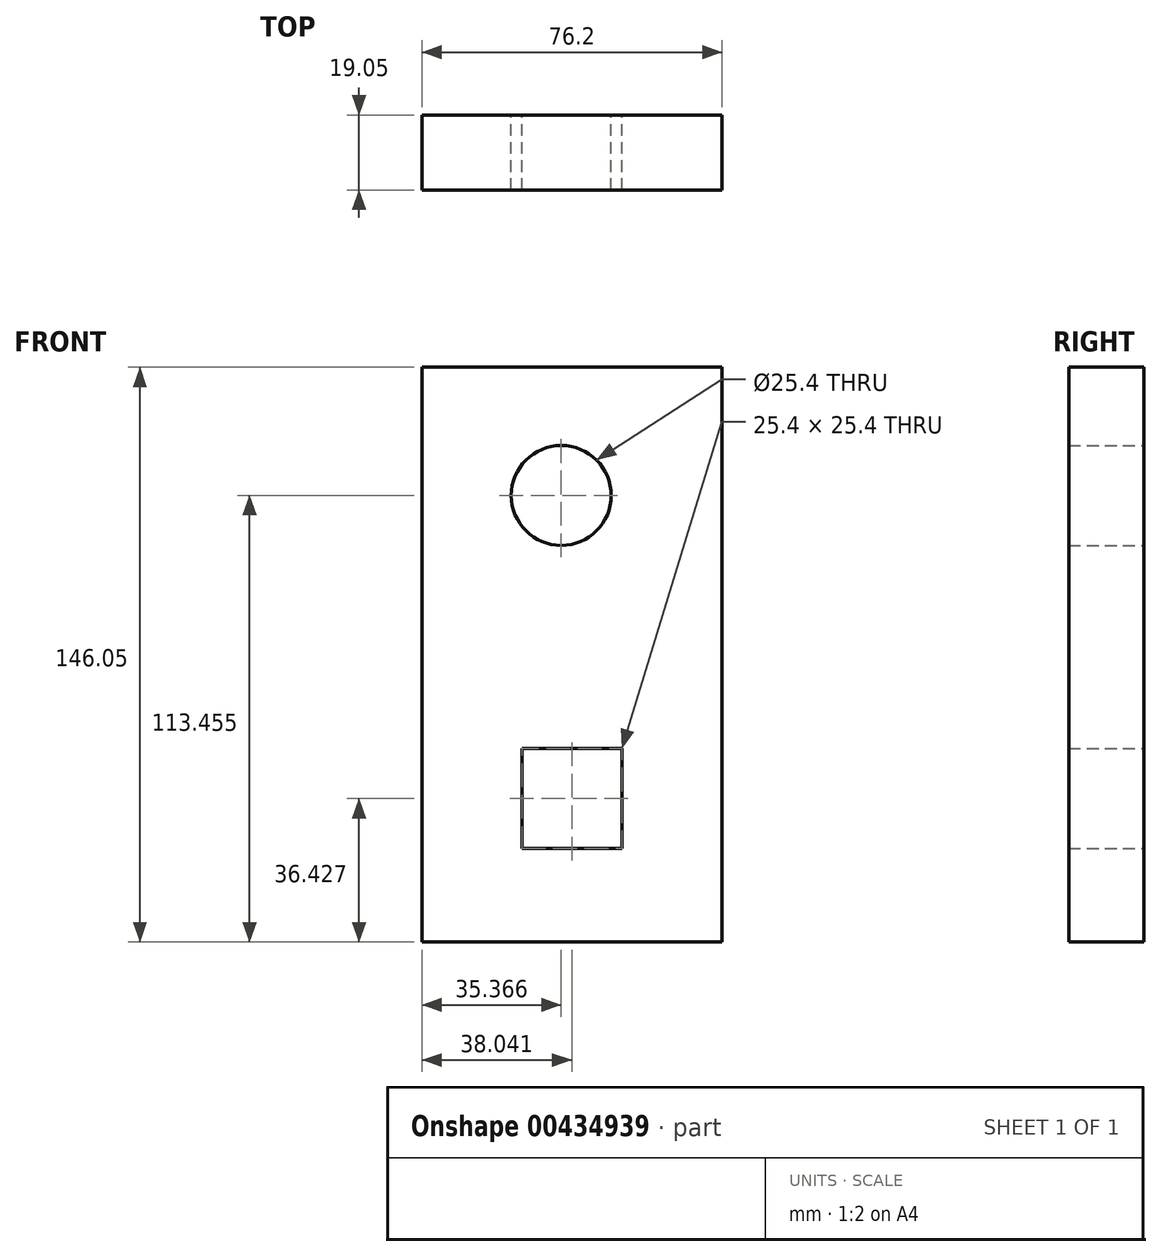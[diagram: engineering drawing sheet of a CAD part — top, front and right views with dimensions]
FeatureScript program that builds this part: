
annotation { "Feature Type Name" : "Feature", "Feature Type Description" : "" }
export const myFeature = defineFeature(function(context is Context, id is Id, definition is map)
    precondition{}
    {
        {
            var Q0;
            Q0=qCreatedBy(makeId("Front.planeOp"),FACE);
            var sketch = newSketch(context, id + "F0", { "sketchPlane" : qUnion([Q0])});
            skLineSegment(sketch, "E0", {"start": v(0, 0) * mm, "end": v(76.2, 0) * mm});
            skLineSegment(sketch, "E1", {"start": v(76.2, 0) * mm, "end": v(76.2, 146.05) * mm});
            skLineSegment(sketch, "E2", {"start": v(76.2, 146.05) * mm, "end": v(0, 146.05) * mm});
            skLineSegment(sketch, "E3", {"start": v(0, 146.05) * mm, "end": v(0, 0) * mm});
            skCircle(sketch, "E4", {"center": v(35.37, 113.46) * mm, "radius": 12.7 * mm});
            skLineSegment(sketch, "E5", {"start": v(25.34, 49.13) * mm, "end": v(50.74, 49.13) * mm});
            skLineSegment(sketch, "E6", {"start": v(50.74, 49.13) * mm, "end": v(50.74, 23.73) * mm});
            skLineSegment(sketch, "E7", {"start": v(50.74, 23.73) * mm, "end": v(25.34, 23.73) * mm});
            skLineSegment(sketch, "E8", {"start": v(25.34, 23.73) * mm, "end": v(25.34, 49.13) * mm});
            skSolve(sketch);
        }
        {
            var Q0;
            Q0=makeQuery(id+"F0.imprint","IMPRINT",FACE,{"disambiguationData":[TD([[makeQuery(id+"F0.imprint","IMPRINT",EDGE,{"derivedFrom":sQuery(id+"F0.wireOp",EDGE,"E0")}),1.0]])]});
            extrude(context, id + "F1", {"entities" : qUnion([Q0]), "depth" : 19.05 * mm});
        }
    });
